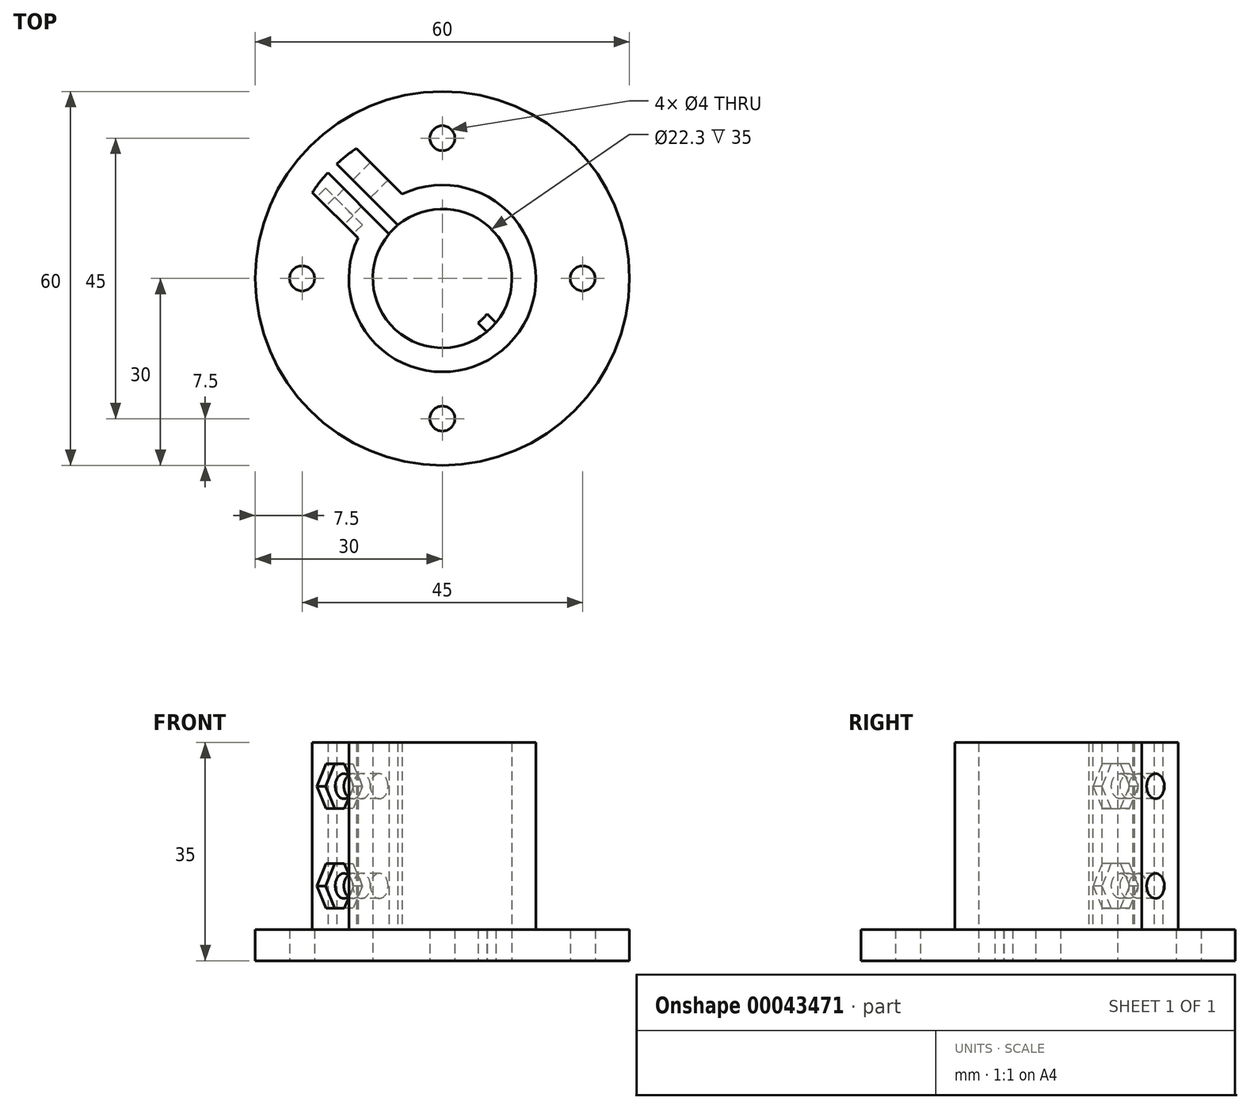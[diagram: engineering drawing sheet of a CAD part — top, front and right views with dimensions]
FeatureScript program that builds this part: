
annotation { "Feature Type Name" : "Feature", "Feature Type Description" : "" }
export const myFeature = defineFeature(function(context is Context, id is Id, definition is map)
    precondition{}
    {
        {
            var Q0;
            Q0=qCreatedBy(makeId("Top.planeOp"),FACE);
            var sketch = newSketch(context, id + "F0", { "sketchPlane" : qUnion([Q0])});
            skCircle(sketch, "E0", {"center": v(0, 0) * mm, "radius": 11.15 * mm});
            skCircle(sketch, "E1", {"center": v(0, 0) * mm, "radius": 30 * mm});
            skArc(sketch, "E2", {"start": v(-11.3, 9.88) * mm, "mid": v(10.6, -10.6) * mm, "end": v(-9.88, 11.3) * mm});
            skCircle(sketch, "E3", {"center": v(-22.5, 0) * mm, "radius": 2 * mm});
            skCircle(sketch, "E4", {"center": v(0, 22.5) * mm, "radius": 2 * mm});
            skCircle(sketch, "E5", {"center": v(22.5, 0) * mm, "radius": 2 * mm});
            skCircle(sketch, "E6", {"center": v(0, -22.5) * mm, "radius": 2 * mm});
            skArc(sketch, "E7", {"start": v(-13.78, 20.86) * mm, "mid": v(-17.68, 17.68) * mm, "end": v(-20.86, 13.78) * mm});
            skLineSegment(sketch, "E8", {"start": v(0, -22.5) * mm, "end": v(1.41, -21.09) * mm, "construction": true});
            skLineSegment(sketch, "E9.trimOffspring", {"start": v(21.09, -1.41) * mm, "end": v(22.5, 0) * mm, "construction": true});
            skLineSegment(sketch, "E10", {"start": v(-7.88, 7.88) * mm, "end": v(-17.68, 17.68) * mm, "construction": true});
            skLineSegment(sketch, "E11", {"start": v(-8.56, 7.15) * mm, "end": v(-18.37, 16.96) * mm});
            skLineSegment(sketch, "E12", {"start": v(-7.15, 8.56) * mm, "end": v(-16.96, 18.37) * mm});
            skLineSegment(sketch, "E13", {"start": v(-13.54, 6.46) * mm, "end": v(-20.86, 13.78) * mm});
            skLineSegment(sketch, "E14", {"start": v(-6.46, 13.54) * mm, "end": v(-13.78, 20.86) * mm});
            skArc(sketch, "E15", {"start": v(5.7, -7.16) * mm, "mid": v(6.47, -6.47) * mm, "end": v(7.16, -5.7) * mm});
            skLineSegment(sketch, "E16", {"start": v(5.7, -7.16) * mm, "end": v(7.13, -8.57) * mm});
            skLineSegment(sketch, "E17", {"start": v(7.16, -5.7) * mm, "end": v(8.58, -7.12) * mm});
            skCircle(sketch, "E18", {"center": v(0, 0) * mm, "radius": 22.5 * mm, "construction": true});
            skSolve(sketch);
        }
        {
            var Q0;
            {var subQ0=sQuery(id+"F0.wireOp",EDGE,"E11");var subQ1=sQuery(id+"F0.wireOp",EDGE,"E0");var subQ2=makeQuery(id+"F0.imprint","INTERSECT",VERTEX,{"derivedFrom":[subQ1,subQ0]});Q0=makeQuery(id+"F0.imprint","IMPRINT",FACE,{"disambiguationData":[TD([[makeQuery(id+"F0.imprint","IMPRINT",EDGE,{"disambiguationData":[TD([[subQ2,-1.0]])],"derivedFrom":subQ1}),-1.0]])]});}
            var Q1;
            {var subQ5=sQuery(id+"F0.wireOp",EDGE,"E13");Q1=makeQuery(id+"F0.imprint","IMPRINT",FACE,{"disambiguationData":[TD([[makeQuery(id+"F0.imprint","IMPRINT",EDGE,{"derivedFrom":subQ5}),-1.0]])]});}
            var Q2;
            {var subQ5=sQuery(id+"F0.wireOp",EDGE,"E14");Q2=makeQuery(id+"F0.imprint","IMPRINT",FACE,{"disambiguationData":[TD([[makeQuery(id+"F0.imprint","IMPRINT",EDGE,{"derivedFrom":subQ5}),1.0]])]});}
            extrude(context, id + "F1", {"entities" : qUnion([Q0, Q1, Q2]), "depth" : 35 * mm});
        }
        {
            var Q0;
            Q0=makeQuery(id+"F0.imprint","IMPRINT",FACE,{"disambiguationData":[TD([[makeQuery(id+"F0.imprint","IMPRINT",EDGE,{"derivedFrom":sQuery(id+"F0.wireOp",EDGE,"E1")}),1.0]])]});
            var Q1;
            Q1=makeQuery(id+"F0.imprint","IMPRINT",FACE,{"disambiguationData":[TD([[makeQuery(id+"F0.imprint","IMPRINT",EDGE,{"derivedFrom":sQuery(id+"F0.wireOp",EDGE,"E15")}),-1.0]])]});
            var Q2;
            {var subQ5=sQuery(id+"F0.wireOp",EDGE,"E0");var subQ7=sQuery(id+"F0.wireOp",EDGE,"E11");var subQ8=makeQuery(id+"F0.imprint","INTERSECT",VERTEX,{"derivedFrom":[subQ5,subQ7]});Q2=makeQuery(id+"F0.imprint","IMPRINT",FACE,{"disambiguationData":[TD([[makeQuery(id+"F0.imprint","IMPRINT",EDGE,{"disambiguationData":[TD([[subQ8,1.0]])],"derivedFrom":subQ5}),-1.0]])]});}
            extrude(context, id + "F2", {"entities" : qUnion([Q0, Q1, Q2]), "operationType" : NewBodyOperationType.ADD, "depth" : 5 * mm});
        }
        {
            var Q0;
            Q0=makeQuery(id+"F1.opExtrude","SWEPT_FACE",FACE,{"disambiguationData":[OSD([sQuery(id+"F0.wireOp",EDGE,"E13")])]});
            cPlane(context, id + "F3", {"entities" : qUnion([Q0]), "cplaneType" : CPlaneType.OFFSET, "offset" : 0 * mm, "width" : 150 * mm, "height" : 150 * mm});
        }
        {
            var Q0;
            Q0=qCreatedBy(id+"F3.planeOp",FACE);
            var sketch = newSketch(context, id + "F4", { "sketchPlane" : qUnion([Q0])});
            skLineSegment(sketch, "E19.0", {"start": v(-14.14, 35) * mm, "end": v(-24.5, 35) * mm});
            skLineSegment(sketch, "E20.0", {"start": v(-14.14, 5) * mm, "end": v(-24.5, 5) * mm});
            skCircle(sketch, "E21", {"center": v(-19.32, 28) * mm, "radius": 2 * mm});
            skCircle(sketch, "E22", {"center": v(-19.32, 12) * mm, "radius": 2 * mm});
            skCircle(sketch, "E23.cCircle", {"center": v(-19.32, 28) * mm, "radius": 3.6 * mm, "construction": true});
            skLineSegment(sketch, "E23.0", {"start": v(-21.4, 31.6) * mm, "end": v(-17.24, 31.6) * mm});
            skLineSegment(sketch, "E23.1", {"start": v(-17.24, 31.6) * mm, "end": v(-15.16, 28) * mm});
            skLineSegment(sketch, "E23.2", {"start": v(-15.16, 28) * mm, "end": v(-17.24, 24.4) * mm});
            skLineSegment(sketch, "E23.3", {"start": v(-17.24, 24.4) * mm, "end": v(-21.4, 24.4) * mm});
            skLineSegment(sketch, "E23.4", {"start": v(-21.4, 24.4) * mm, "end": v(-23.48, 28) * mm});
            skLineSegment(sketch, "E23.5", {"start": v(-23.48, 28) * mm, "end": v(-21.4, 31.6) * mm});
            skPoint(sketch, "E23.0.midPoint", {"position": v(-19.32, 31.6) * mm});
            skCircle(sketch, "E24.cCircle", {"center": v(-19.32, 12) * mm, "radius": 3.6 * mm, "construction": true});
            skLineSegment(sketch, "E24.0", {"start": v(-21.4, 15.6) * mm, "end": v(-17.24, 15.6) * mm});
            skLineSegment(sketch, "E24.1", {"start": v(-17.24, 15.6) * mm, "end": v(-15.16, 12) * mm});
            skLineSegment(sketch, "E24.2", {"start": v(-15.16, 12) * mm, "end": v(-17.24, 8.4) * mm});
            skLineSegment(sketch, "E24.3", {"start": v(-17.24, 8.4) * mm, "end": v(-21.4, 8.4) * mm});
            skLineSegment(sketch, "E24.4", {"start": v(-21.4, 8.4) * mm, "end": v(-23.48, 12) * mm});
            skLineSegment(sketch, "E24.5", {"start": v(-23.48, 12) * mm, "end": v(-21.4, 15.6) * mm});
            skPoint(sketch, "E24.0.midPoint", {"position": v(-19.32, 15.6) * mm});
            skPoint(sketch, "E25.orphan", {"position": v(-19.32, 35) * mm});
            skPoint(sketch, "E26.trimOffspring.end.orphan", {"position": v(-19.32, 5) * mm});
            skSolve(sketch);
        }
        {
            var Q0;
            Q0=makeQuery(id+"F4.imprint","IMPRINT",FACE,{"disambiguationData":[TD([[makeQuery(id+"F4.imprint","IMPRINT",EDGE,{"derivedFrom":sQuery(id+"F4.wireOp",EDGE,"E21")}),1.0]])]});
            var Q1;
            Q1=makeQuery(id+"F4.imprint","IMPRINT",FACE,{"disambiguationData":[TD([[makeQuery(id+"F4.imprint","IMPRINT",EDGE,{"derivedFrom":sQuery(id+"F4.wireOp",EDGE,"E22")}),1.0]])]});
            extrude(context, id + "F5", {"entities" : qUnion([Q0, Q1]), "operationType" : NewBodyOperationType.REMOVE, "oppositeDirection" : true, "depth" : 11 * mm});
        }
        {
            var Q0;
            Q0=makeQuery(id+"F4.imprint","IMPRINT",FACE,{"disambiguationData":[TD([[makeQuery(id+"F4.imprint","IMPRINT",EDGE,{"derivedFrom":sQuery(id+"F4.wireOp",EDGE,"E21")}),-1.0]])]});
            var Q1;
            Q1=makeQuery(id+"F4.imprint","IMPRINT",FACE,{"disambiguationData":[TD([[makeQuery(id+"F4.imprint","IMPRINT",EDGE,{"derivedFrom":sQuery(id+"F4.wireOp",EDGE,"E22")}),-1.0]])]});
            extrude(context, id + "F6", {"entities" : qUnion([Q0, Q1]), "operationType" : NewBodyOperationType.REMOVE, "oppositeDirection" : true, "depth" : 2 * mm});
        }
    });
